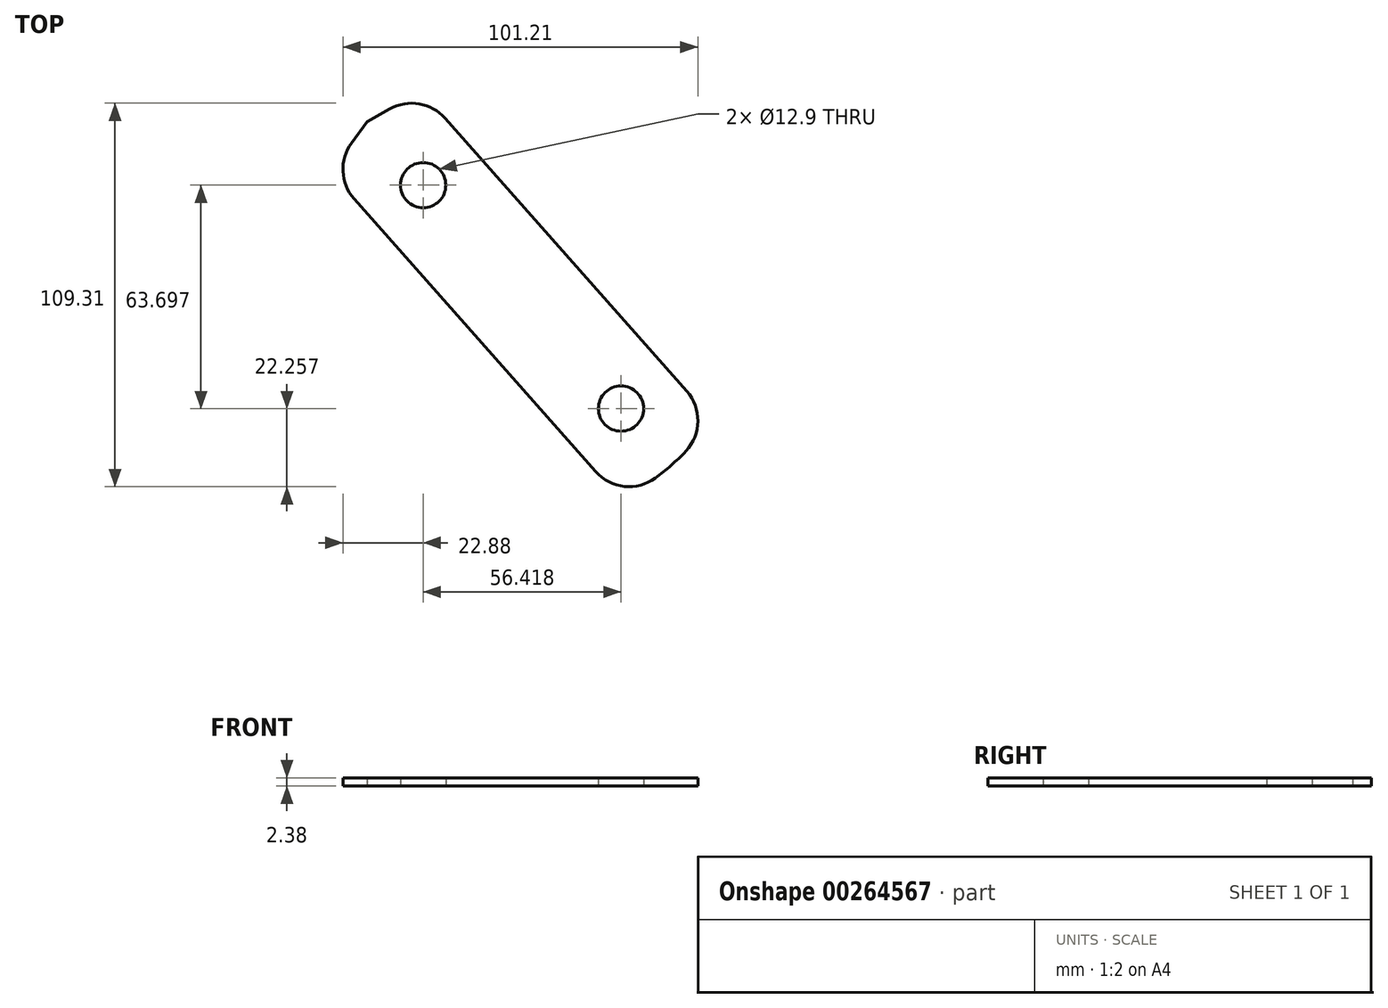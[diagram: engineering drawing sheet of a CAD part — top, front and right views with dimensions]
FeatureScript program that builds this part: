
annotation { "Feature Type Name" : "Feature", "Feature Type Description" : "" }
export const myFeature = defineFeature(function(context is Context, id is Id, definition is map)
    precondition{}
    {
        {
            var Q0;
            Q0=qCreatedBy(makeId("Top.planeOp"),FACE);
            var sketch = newSketch(context, id + "F0", { "sketchPlane" : qUnion([Q0])});
            skLineSegment(sketch, "E0", {"start": v(-12.95, -11.5) * mm, "end": v(12.98, 11.47) * mm});
            skLineSegment(sketch, "E1.MirrorCS", {"start": v(23.64, 20.9) * mm, "end": v(23.63, 20.91) * mm});
            skLineSegment(sketch, "E2.MirrorCS", {"start": v(23.63, 20.91) * mm, "end": v(23.64, 20.9) * mm});
            skArc(sketch, "E3.trimOffspring", {"start": v(37.6, -51.17) * mm, "mid": v(42.1, -47.53) * mm, "end": v(46.25, -43.5) * mm});
            skLineSegment(sketch, "E4", {"start": v(0, 0) * mm, "end": v(42.1, -47.53) * mm});
            skLineSegment(sketch, "E5", {"start": v(0, 0) * mm, "end": v(-44.63, 50.39) * mm});
            skCircle(sketch, "E6", {"center": v(-28.63, 32.32) * mm, "radius": 6.45 * mm});
            skLineSegment(sketch, "E7", {"start": v(-28.63, 32.32) * mm, "end": v(27.79, -31.37) * mm});
            skCircle(sketch, "E8", {"center": v(27.79, -31.37) * mm, "radius": 6.45 * mm});
            skLineSegment(sketch, "E9", {"start": v(-22.38, 51.4) * mm, "end": v(46.51, -26.38) * mm});
            skLineSegment(sketch, "E10.MirrorCS", {"start": v(-48.32, 28.42) * mm, "end": v(20.58, -49.36) * mm});
            skPoint(sketch, "E11.visualSharp", {"position": v(53.47, -34.25) * mm});
            skArc(sketch, "E11.filletArc", {"start": v(46.25, -43.5) * mm, "mid": v(49.7, -35) * mm, "end": v(46.51, -26.38) * mm});
            skPoint(sketch, "E12.visualSharp", {"position": v(27.54, -57.22) * mm});
            skArc(sketch, "E12.filletArc", {"start": v(20.58, -49.36) * mm, "mid": v(28.74, -53.56) * mm, "end": v(37.6, -51.17) * mm});
            skLineSegment(sketch, "E13", {"start": v(-44.63, 50.39) * mm, "end": v(-38.1, 54.05) * mm});
            skLineSegment(sketch, "E14", {"start": v(-49.05, 44.36) * mm, "end": v(-44.63, 50.39) * mm});
            skPoint(sketch, "E15.visualSharp", {"position": v(-55.1, 36.1) * mm});
            skArc(sketch, "E15.filletArc", {"start": v(-49.05, 44.36) * mm, "mid": v(-51.5, 36.26) * mm, "end": v(-48.32, 28.42) * mm});
            skPoint(sketch, "E16.visualSharp", {"position": v(-29.18, 59.06) * mm});
            skArc(sketch, "E16.filletArc", {"start": v(-22.38, 51.4) * mm, "mid": v(-29.78, 55.5) * mm, "end": v(-38.1, 54.05) * mm});
            skPoint(sketch, "E17", {"position": v(-22.31, 25.2) * mm});
            skPoint(sketch, "E18", {"position": v(23.51, -26.54) * mm});
            skPoint(sketch, "E19", {"position": v(-24.35, 27.5) * mm});
            skSolve(sketch);
        }
        {
            var Q0;
            Q0=makeQuery(id+"F0.imprint","IMPRINT",FACE,{"disambiguationData":[TD([[makeQuery(id+"F0.imprint","IMPRINT",EDGE,{"derivedFrom":sQuery(id+"F0.wireOp",EDGE,"W9ZEXt3y-tTaE-D2W9-7RGd-zofzFIt2jUyi")}),1.0]])]});
            var Q1;
            {var subQ0=sQuery(id+"F0.wireOp",EDGE,"E0");Q1=makeQuery(id+"F0.imprint","IMPRINT",FACE,{"disambiguationData":[TD([[makeQuery(id+"F0.imprint","IMPRINT",EDGE,{"derivedFrom":subQ0}),-1.0]])]});}
            var Q2;
            Q2=makeQuery(id+"F0.imprint","IMPRINT",FACE,{"disambiguationData":[TD([[makeQuery(id+"F0.imprint","IMPRINT",EDGE,{"derivedFrom":sQuery(id+"F0.wireOp",EDGE,"E0")}),1.0]])]});
            var Q3;
            {var subQ0=sQuery(id+"F0.wireOp",EDGE,"E3.trimOffspring");Q3=makeQuery(id+"F0.imprint","IMPRINT",FACE,{"disambiguationData":[TD([[makeQuery(id+"F0.imprint","IMPRINT",EDGE,{"derivedFrom":subQ0}),1.0]])]});}
            extrude(context, id + "F1", {"entities" : qUnion([Q0, Q1, Q2, Q3]), "depth" : 2.38 * mm});
        }
    });
